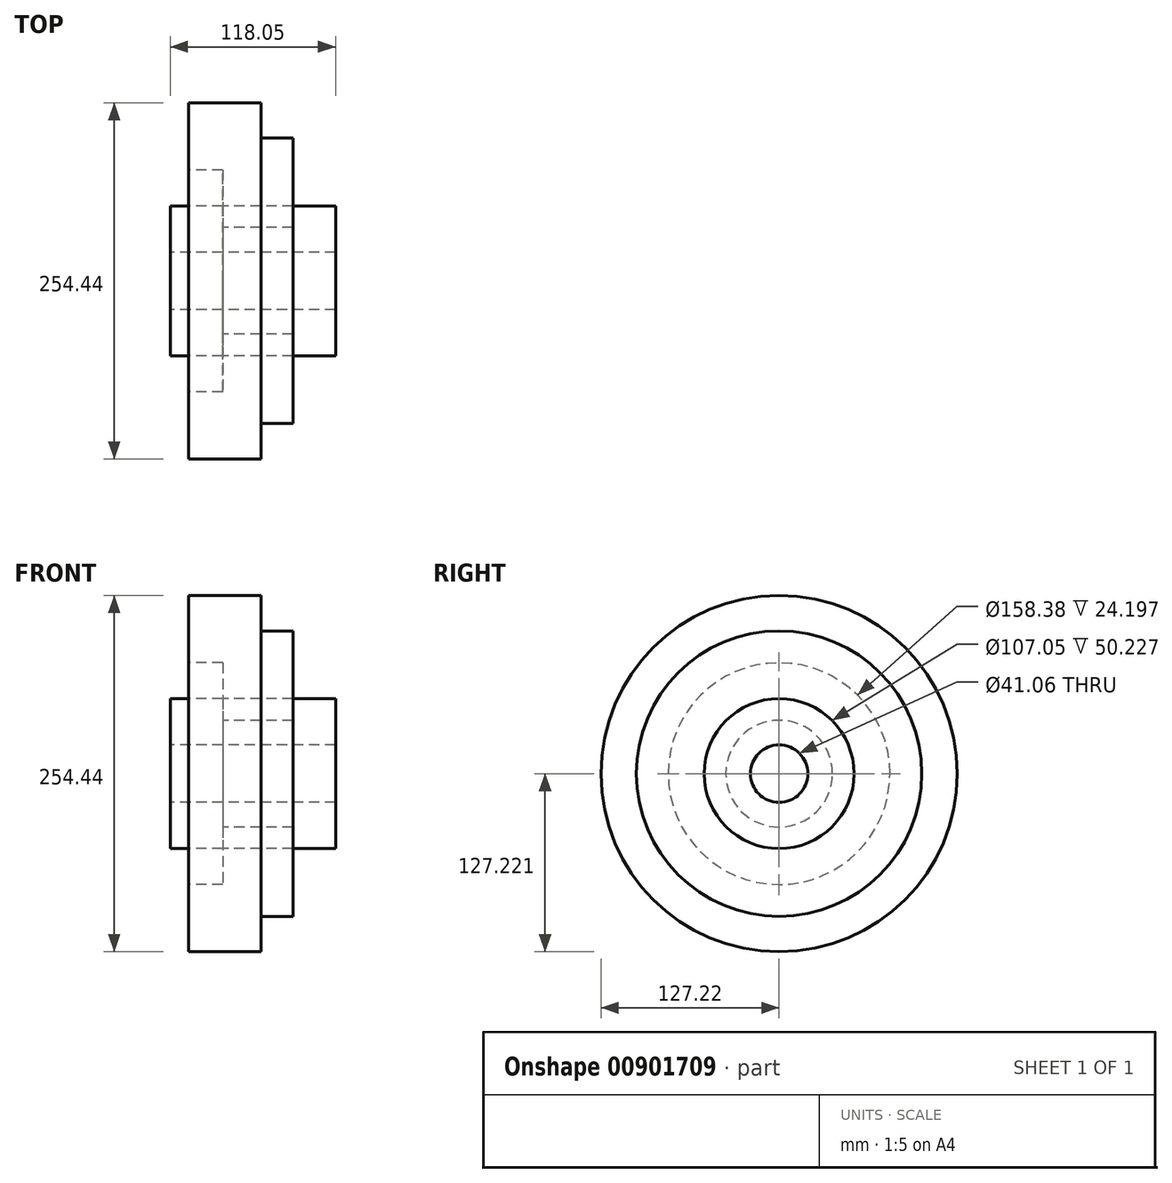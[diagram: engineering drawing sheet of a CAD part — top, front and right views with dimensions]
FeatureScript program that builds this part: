
annotation { "Feature Type Name" : "Feature", "Feature Type Description" : "" }
export const myFeature = defineFeature(function(context is Context, id is Id, definition is map)
    precondition{}
    {
        {
            var Q0;
            Q0=qCreatedBy(makeId("Front.planeOp"),FACE);
            var sketch = newSketch(context, id + "F0", { "sketchPlane" : qUnion([Q0])});
            skLineSegment(sketch, "E0.bottom", {"start": v(-51.7, 48.03) * mm, "end": v(0, 48.03) * mm});
            skLineSegment(sketch, "E0.top", {"start": v(-51.7, 0) * mm, "end": v(0, 0) * mm});
            skLineSegment(sketch, "E0.left", {"start": v(-51.7, 48.03) * mm, "end": v(-51.7, 0) * mm});
            skLineSegment(sketch, "E0.right", {"start": v(0, 48.03) * mm, "end": v(0, 0) * mm});
            skLineSegment(sketch, "E1.bottom", {"start": v(-27.5, 22.73) * mm, "end": v(22.73, 22.73) * mm});
            skLineSegment(sketch, "E1.top", {"start": v(-27.5, -41.06) * mm, "end": v(22.73, -41.06) * mm});
            skLineSegment(sketch, "E1.left", {"start": v(-27.5, 22.73) * mm, "end": v(-27.5, -41.06) * mm});
            skLineSegment(sketch, "E1.right", {"start": v(22.73, 22.73) * mm, "end": v(22.73, -41.06) * mm});
            skLineSegment(sketch, "E2.bottom", {"start": v(-64.9, -25.66) * mm, "end": v(53.16, -25.66) * mm});
            skLineSegment(sketch, "E2.top", {"start": v(-64.9, -58.66) * mm, "end": v(53.16, -58.66) * mm});
            skLineSegment(sketch, "E2.left", {"start": v(-64.9, -25.66) * mm, "end": v(-64.9, -58.66) * mm});
            skLineSegment(sketch, "E2.right", {"start": v(53.16, -25.66) * mm, "end": v(53.16, -58.66) * mm});
            skLineSegment(sketch, "E3", {"start": v(-77.72, -79.19) * mm, "end": v(84.32, -79.19) * mm});
            skSolve(sketch);
        }
        {
            var Q0;
            {var subQ0=sQuery(id+"F0.wireOp",EDGE,"E0.right");var subQ1=sQuery(id+"F0.wireOp",EDGE,"E0.top");var subQ2=makeQuery(id+"F0.imprint","INTERSECT",VERTEX,{"derivedFrom":[subQ1,subQ0]});Q0=makeQuery(id+"F0.imprint","IMPRINT",FACE,{"disambiguationData":[TD([[makeQuery(id+"F0.imprint","IMPRINT",EDGE,{"disambiguationData":[TD([[subQ2,1.0]])],"derivedFrom":subQ1}),1.0]])]});}
            var Q1;
            {var subQ1=sQuery(id+"F0.wireOp",EDGE,"E0.bottom");Q1=makeQuery(id+"F0.imprint","IMPRINT",FACE,{"disambiguationData":[TD([[makeQuery(id+"F0.imprint","IMPRINT",EDGE,{"derivedFrom":subQ1}),-1.0]])]});}
            var Q2;
            {var subQ1=sQuery(id+"F0.wireOp",EDGE,"E0.top");var subQ5=sQuery(id+"F0.wireOp",EDGE,"E0.right");var subQ6=makeQuery(id+"F0.imprint","INTERSECT",VERTEX,{"derivedFrom":[subQ1,subQ5]});Q2=makeQuery(id+"F0.imprint","IMPRINT",FACE,{"disambiguationData":[TD([[makeQuery(id+"F0.imprint","IMPRINT",EDGE,{"disambiguationData":[TD([[subQ6,1.0]])],"derivedFrom":subQ1}),-1.0]])]});}
            var Q3;
            {var subQ4=sQuery(id+"F0.wireOp",EDGE,"E1.top");Q3=makeQuery(id+"F0.imprint","IMPRINT",FACE,{"disambiguationData":[TD([[makeQuery(id+"F0.imprint","IMPRINT",EDGE,{"derivedFrom":subQ4}),-1.0]])]});}
            var Q4;
            Q4=sQuery(id+"F0.wireOp",EDGE,"E3");
            revolve(context, id + "F1", {"surfaceOperationType" : NewSurfaceOperationType.NEW, "entities" : qUnion([Q0, Q1, Q2, Q3]), "axis" : qUnion([Q4]), "revolveType" : RevolveType.FULL});
        }
    });
